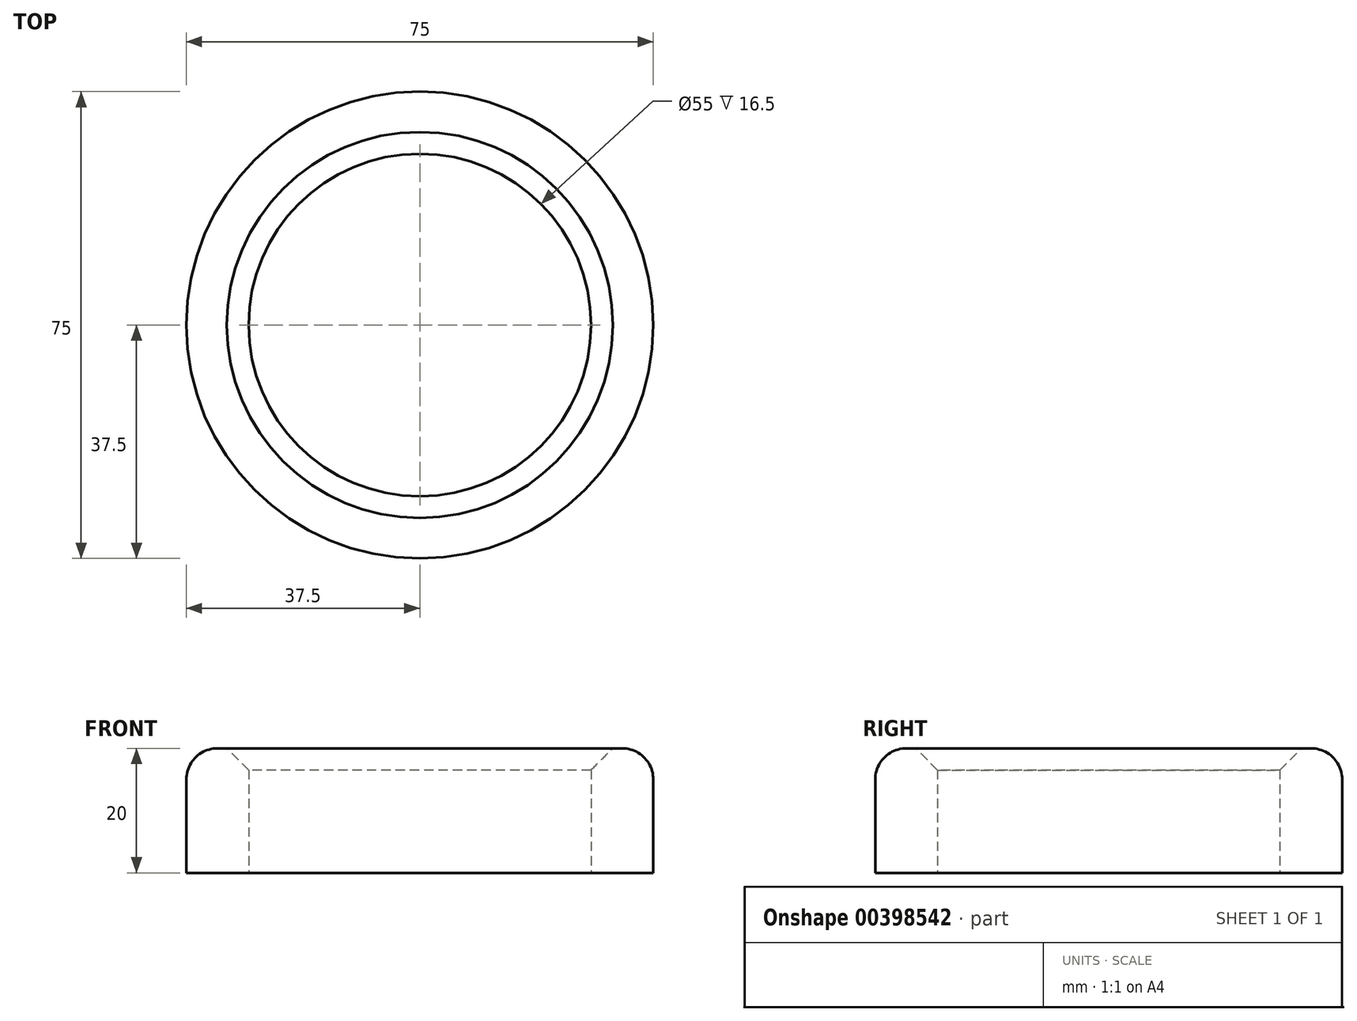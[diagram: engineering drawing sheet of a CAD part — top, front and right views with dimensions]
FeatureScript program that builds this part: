
annotation { "Feature Type Name" : "Feature", "Feature Type Description" : "" }
export const myFeature = defineFeature(function(context is Context, id is Id, definition is map)
    precondition{}
    {
        {
            var Q0;
            Q0=qCreatedBy(makeId("Top.planeOp"),FACE);
            var sketch = newSketch(context, id + "F0", { "sketchPlane" : qUnion([Q0])});
            skCircle(sketch, "E0", {"center": v(0, 0) * mm, "radius": 27.5 * mm});
            skCircle(sketch, "E1", {"center": v(0, 0) * mm, "radius": 37.5 * mm});
            skSolve(sketch);
        }
        {
            var Q0;
            Q0=makeQuery(id+"F0.imprint","IMPRINT",FACE,{"disambiguationData":[TD([[makeQuery(id+"F0.imprint","IMPRINT",EDGE,{"derivedFrom":sQuery(id+"F0.wireOp",EDGE,"E0")}),-1.0]])]});
            extrude(context, id + "F1", {"entities" : qUnion([Q0]), "depth" : 20 * mm});
        }
        {
            var Q0;
            Q0=makeQuery(id+"F1.opExtrude","CAP_EDGE",EDGE,{"disambiguationData":[OSD([sQuery(id+"F0.wireOp",EDGE,"E0")])],"isStart":false});
            chamfer(context, id + "F2", {"entities" : qUnion([Q0]), "width" : 3.5 * mm, "tangentPropagation" : true});
        }
        {
            var Q0;
            Q0=makeQuery(id+"F1.opExtrude","CAP_EDGE",EDGE,{"disambiguationData":[OSD([sQuery(id+"F0.wireOp",EDGE,"E1")])],"isStart":false});
            fillet(context, id + "F3", {"entities" : qUnion([Q0]), "radius" : 5 * mm, "tangentPropagation" : true, "allowEdgeOverflow" : false});
        }
    });
